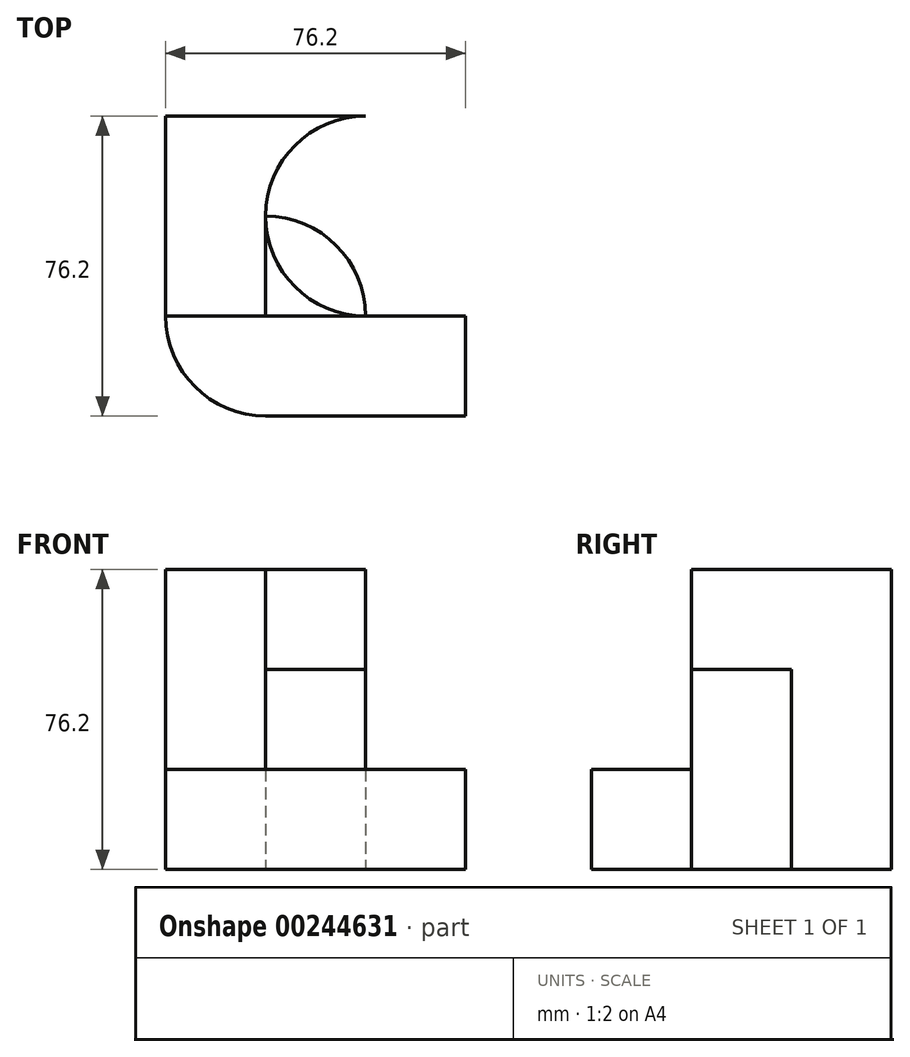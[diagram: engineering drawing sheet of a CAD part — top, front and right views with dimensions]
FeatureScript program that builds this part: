
annotation { "Feature Type Name" : "Feature", "Feature Type Description" : "" }
export const myFeature = defineFeature(function(context is Context, id is Id, definition is map)
    precondition{}
    {
        {
            var Q0;
            Q0=qCreatedBy(makeId("Top.planeOp"),FACE);
            var sketch = newSketch(context, id + "F0", { "sketchPlane" : qUnion([Q0])});
            skLineSegment(sketch, "E0.bottom", {"start": v(0, 0) * mm, "end": v(25.4, 0) * mm});
            skLineSegment(sketch, "E0.top", {"start": v(0, 25.4) * mm, "end": v(25.4, 25.4) * mm});
            skLineSegment(sketch, "E0.left", {"start": v(0, 0) * mm, "end": v(0, 25.4) * mm});
            skLineSegment(sketch, "E0.right", {"start": v(25.4, 0) * mm, "end": v(25.4, 25.4) * mm});
            skLineSegment(sketch, "E1.top", {"start": v(0, 50.8) * mm, "end": v(25.4, 50.8) * mm});
            skLineSegment(sketch, "E1.left", {"start": v(0, 25.4) * mm, "end": v(0, 50.8) * mm});
            skLineSegment(sketch, "E1.right", {"start": v(25.4, 25.4) * mm, "end": v(25.4, 50.8) * mm});
            skLineSegment(sketch, "E2.top", {"start": v(0, 76.2) * mm, "end": v(25.4, 76.2) * mm});
            skLineSegment(sketch, "E2.left", {"start": v(0, 50.8) * mm, "end": v(0, 76.2) * mm});
            skLineSegment(sketch, "E2.right", {"start": v(25.4, 50.8) * mm, "end": v(25.4, 76.2) * mm});
            skLineSegment(sketch, "E3.bottom", {"start": v(25.4, 76.2) * mm, "end": v(50.8, 76.2) * mm});
            skLineSegment(sketch, "E3.top", {"start": v(25.4, 50.8) * mm, "end": v(50.8, 50.8) * mm});
            skLineSegment(sketch, "E3.left", {"start": v(25.4, 76.2) * mm, "end": v(25.4, 50.8) * mm});
            skLineSegment(sketch, "E3.right", {"start": v(50.8, 76.2) * mm, "end": v(50.8, 50.8) * mm});
            skLineSegment(sketch, "E4.bottom", {"start": v(50.8, 50.8) * mm, "end": v(25.4, 50.8) * mm});
            skLineSegment(sketch, "E4.top", {"start": v(50.8, 25.4) * mm, "end": v(25.4, 25.4) * mm});
            skLineSegment(sketch, "E4.left", {"start": v(50.8, 50.8) * mm, "end": v(50.8, 25.4) * mm});
            skLineSegment(sketch, "E4.right", {"start": v(25.4, 50.8) * mm, "end": v(25.4, 25.4) * mm});
            skLineSegment(sketch, "E5.top", {"start": v(50.8, 0) * mm, "end": v(25.4, 0) * mm});
            skLineSegment(sketch, "E5.left", {"start": v(50.8, 25.4) * mm, "end": v(50.8, 0) * mm});
            skLineSegment(sketch, "E5.right", {"start": v(25.4, 25.4) * mm, "end": v(25.4, 0) * mm});
            skLineSegment(sketch, "E6.bottom", {"start": v(50.8, 0) * mm, "end": v(76.2, 0) * mm});
            skLineSegment(sketch, "E6.top", {"start": v(50.8, 25.4) * mm, "end": v(76.2, 25.4) * mm});
            skLineSegment(sketch, "E6.left", {"start": v(50.8, 0) * mm, "end": v(50.8, 25.4) * mm});
            skLineSegment(sketch, "E6.right", {"start": v(76.2, 0) * mm, "end": v(76.2, 25.4) * mm});
            skLineSegment(sketch, "E7.bottom", {"start": v(76.2, 25.4) * mm, "end": v(50.8, 25.4) * mm});
            skLineSegment(sketch, "E7.top", {"start": v(76.2, 50.8) * mm, "end": v(50.8, 50.8) * mm});
            skLineSegment(sketch, "E7.left", {"start": v(76.2, 25.4) * mm, "end": v(76.2, 50.8) * mm});
            skLineSegment(sketch, "E7.right", {"start": v(50.8, 25.4) * mm, "end": v(50.8, 50.8) * mm});
            skLineSegment(sketch, "E8.bottom", {"start": v(50.8, 50.8) * mm, "end": v(76.2, 50.8) * mm});
            skLineSegment(sketch, "E8.top", {"start": v(50.8, 76.2) * mm, "end": v(76.2, 76.2) * mm});
            skLineSegment(sketch, "E8.left", {"start": v(50.8, 50.8) * mm, "end": v(50.8, 76.2) * mm});
            skLineSegment(sketch, "E8.right", {"start": v(76.2, 50.8) * mm, "end": v(76.2, 76.2) * mm});
            skCircle(sketch, "E9", {"center": v(25.4, 25.4) * mm, "radius": 25.4 * mm});
            skCircle(sketch, "E10", {"center": v(50.8, 50.8) * mm, "radius": 25.4 * mm});
            skSolve(sketch);
        }
        {
            var Q0;
            Q0=makeQuery(id+"F0.imprint","IMPRINT",FACE,{"disambiguationData":[TD([[makeQuery(id+"F0.imprint","IMPRINT",EDGE,{"derivedFrom":sQuery(id+"F0.wireOp",EDGE,"E1.top")}),1.0]])]});
            var Q1;
            {var subQ0=sQuery(id+"F0.wireOp",EDGE,"E0.top");Q1=makeQuery(id+"F0.imprint","IMPRINT",FACE,{"disambiguationData":[TD([[makeQuery(id+"F0.imprint","IMPRINT",EDGE,{"derivedFrom":subQ0}),1.0]])]});}
            var Q2;
            {var subQ0=sQuery(id+"F0.wireOp",EDGE,"E1.left");Q2=makeQuery(id+"F0.imprint","IMPRINT",FACE,{"disambiguationData":[TD([[makeQuery(id+"F0.imprint","IMPRINT",EDGE,{"derivedFrom":subQ0}),-1.0]])]});}
            var Q3;
            {var subQ0=sQuery(id+"F0.wireOp",EDGE,"E4.bottom");Q3=makeQuery(id+"F0.imprint","IMPRINT",FACE,{"disambiguationData":[TD([[makeQuery(id+"F0.imprint","IMPRINT",EDGE,{"derivedFrom":subQ0}),-1.0]])]});}
            var Q4;
            {var subQ0=sQuery(id+"F0.wireOp",EDGE,"E3.bottom");Q4=makeQuery(id+"F0.imprint","IMPRINT",FACE,{"disambiguationData":[TD([[makeQuery(id+"F0.imprint","IMPRINT",EDGE,{"derivedFrom":subQ0}),-1.0]])]});}
            extrude(context, id + "F1", {"entities" : qUnion([Q0, Q1, Q2, Q3, Q4]), "depth" : 76.2 * mm});
        }
        {
            var Q0;
            {var subQ0=sQuery(id+"F0.wireOp",EDGE,"E4.bottom");Q0=makeQuery(id+"F0.imprint","IMPRINT",FACE,{"disambiguationData":[TD([[makeQuery(id+"F0.imprint","IMPRINT",EDGE,{"derivedFrom":subQ0}),1.0]])]});}
            var Q1;
            {var subQ0=sQuery(id+"F0.wireOp",EDGE,"E10");var subQ1=sQuery(id+"F0.wireOp",EDGE,"E9");var subQ2=makeQuery(id+"F0.imprint","INTERSECT",VERTEX,{"derivedFrom":[sQuery(id+"F0.wireOp",EDGE,"E1.top"),sQuery(id+"F0.wireOp",EDGE,"E3.left"),sQuery(id+"F0.wireOp",EDGE,"E4.bottom"),sQuery(id+"F0.wireOp",EDGE,"E4.right"),subQ1,subQ0]});Q1=makeQuery(id+"F0.imprint","IMPRINT",FACE,{"disambiguationData":[TD([[makeQuery(id+"F0.imprint","IMPRINT",EDGE,{"disambiguationData":[TD([[subQ2,1.0]])],"derivedFrom":subQ1}),1.0]])]});}
            var Q2;
            {var subQ0=sQuery(id+"F0.wireOp",EDGE,"E4.right");Q2=makeQuery(id+"F0.imprint","IMPRINT",FACE,{"disambiguationData":[TD([[makeQuery(id+"F0.imprint","IMPRINT",EDGE,{"derivedFrom":subQ0}),1.0]])]});}
            var Q3;
            {var subQ0=sQuery(id+"F0.wireOp",EDGE,"E7.right");Q3=makeQuery(id+"F0.imprint","IMPRINT",FACE,{"disambiguationData":[TD([[makeQuery(id+"F0.imprint","IMPRINT",EDGE,{"derivedFrom":subQ0}),-1.0]])]});}
            var Q4;
            {var subQ0=sQuery(id+"F0.wireOp",EDGE,"E7.bottom");Q4=makeQuery(id+"F0.imprint","IMPRINT",FACE,{"disambiguationData":[TD([[makeQuery(id+"F0.imprint","IMPRINT",EDGE,{"derivedFrom":subQ0}),-1.0]])]});}
            extrude(context, id + "F2", {"entities" : qUnion([Q0, Q1, Q2, Q3, Q4]), "operationType" : NewBodyOperationType.ADD, "depth" : 50.8 * mm});
        }
        {
            var Q0;
            Q0=makeQuery(id+"F0.imprint","IMPRINT",FACE,{"disambiguationData":[TD([[makeQuery(id+"F0.imprint","IMPRINT",EDGE,{"derivedFrom":sQuery(id+"F0.wireOp",EDGE,"E6.bottom")}),1.0]])]});
            var Q1;
            {var subQ0=sQuery(id+"F0.wireOp",EDGE,"E4.top");Q1=makeQuery(id+"F0.imprint","IMPRINT",FACE,{"disambiguationData":[TD([[makeQuery(id+"F0.imprint","IMPRINT",EDGE,{"derivedFrom":subQ0}),1.0]])]});}
            var Q2;
            {var subQ0=sQuery(id+"F0.wireOp",EDGE,"E5.top");Q2=makeQuery(id+"F0.imprint","IMPRINT",FACE,{"disambiguationData":[TD([[makeQuery(id+"F0.imprint","IMPRINT",EDGE,{"derivedFrom":subQ0}),-1.0]])]});}
            var Q3;
            {var subQ0=sQuery(id+"F0.wireOp",EDGE,"E8.bottom");Q3=makeQuery(id+"F0.imprint","IMPRINT",FACE,{"disambiguationData":[TD([[makeQuery(id+"F0.imprint","IMPRINT",EDGE,{"derivedFrom":subQ0}),1.0]])]});}
            var Q4;
            {var subQ0=sQuery(id+"F0.wireOp",EDGE,"E0.top");Q4=makeQuery(id+"F0.imprint","IMPRINT",FACE,{"disambiguationData":[TD([[makeQuery(id+"F0.imprint","IMPRINT",EDGE,{"derivedFrom":subQ0}),-1.0]])]});}
            extrude(context, id + "F3", {"entities" : qUnion([Q0, Q1, Q2, Q3, Q4]), "operationType" : NewBodyOperationType.ADD, "depth" : 25.4 * mm});
        }
    });
